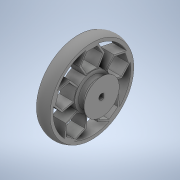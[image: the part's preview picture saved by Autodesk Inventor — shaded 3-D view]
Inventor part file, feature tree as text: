
AUTODESK INVENTOR PART (.ipt)
format: ipt  version: 2020 (Build 240168000, 168)  size: 419,840 bytes
history: native  units: in
note: dims shown in document units (in); Inventor stores cm internally (conversion verified against a paired STEP export)
features: sketch x4, extrude x2, revolve x2, projected_geometry x1
ambient origin geometry x8: Origin, YZ Plane, XZ Plane, XY Plane, X Axis, Y Axis, Z Axis, Center Point
bodies: Solid1 (feature_tree)
feature tree (9):
  extrude  "Extrusion1"  Depth=0.0394in
  sketch  "Sketch3"  dims[d6=0.7087in d7=0.1969in]
  revolve  "Revolution1"  [1 undecoded]
  extrude  "Extrusion2"  Depth=0.1969in
  revolve  "Revolution2"  [1 undecoded]
  sketch  "Sketch1"  dims[d0=0.1181in d1=0.0394in]
  sketch  "Sketch2"  dims[d3=1.6929in d4=0.1181in]
  projected_geometry  "Projected Loop1"
  sketch  "Sketch4"  dims[d8=0.0in d9=1.6929in d10=0.063in d11=0.0315in d16=0.2756in d17=0.0in d19=360.0deg d20=0.0984in d24=0.0394in d25=90.0deg d26=45.0deg d28=0.0079in d29=1.9685in d31=360.0deg]
note: 2 required parameter values undecoded (feature->parameter linkage not recoverable at this tier; creation-order binding heuristic only, values carry confidence <= 0.55)
